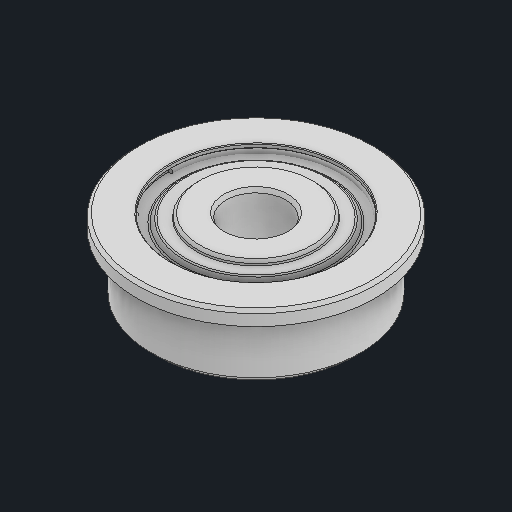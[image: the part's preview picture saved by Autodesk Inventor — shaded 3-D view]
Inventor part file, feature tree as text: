
AUTODESK INVENTOR PART (.ipt)
format: ipt  version: 2024 (Build 280153000, 153)  size: 258,048 bytes
history: native  units: in
note: dims shown in document units (in); Inventor stores cm internally (conversion verified against a paired STEP export)
features: revolve x1, mirror x1, chamfer x1
ambient origin geometry x8: Origin, YZ Plane, XZ Plane, XY Plane, X Axis, Y Axis, Z Axis, Center Point
bodies: Solid1 (feature_tree), Solid2 (feature_tree), Solid3 (feature_tree)
feature tree (3):
  revolve  "Revolve1"  [1 undecoded]
  mirror  "Mirror3"
  chamfer  "Chamfer7"  [1 undecoded]
note: 2 required parameter values undecoded (feature->parameter linkage not recoverable at this tier; creation-order binding heuristic only, values carry confidence <= 0.55)
